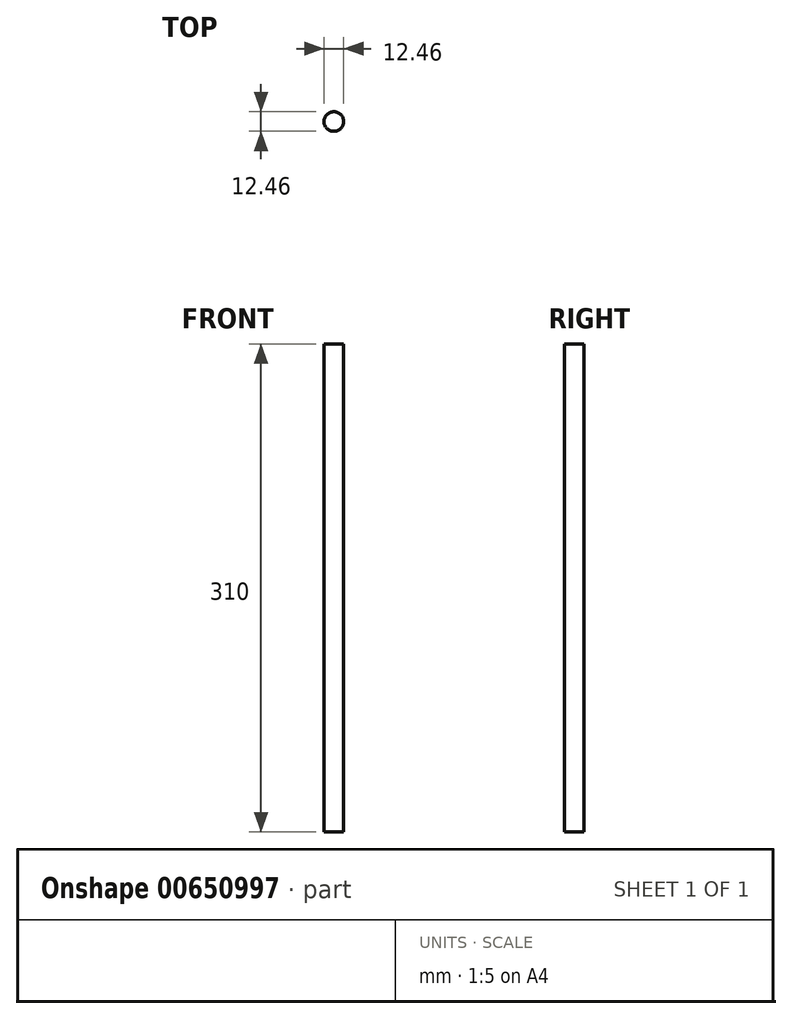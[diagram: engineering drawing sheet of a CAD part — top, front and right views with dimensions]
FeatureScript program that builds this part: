
annotation { "Feature Type Name" : "Feature", "Feature Type Description" : "" }
export const myFeature = defineFeature(function(context is Context, id is Id, definition is map)
    precondition{}
    {
        {
            var Q0;
            Q0=qCreatedBy(makeId("Top.planeOp"),FACE);
            var sketch = newSketch(context, id + "F0", { "sketchPlane" : qUnion([Q0])});
            skCircle(sketch, "E0", {"center": v(-15.14, -11.46) * mm, "radius": 6.23 * mm});
            skSolve(sketch);
        }
        {
            var Q0;
            Q0 = qSketchRegion(id + "F0", true);
            extrude(context, id + "F1", {"entities" : qUnion([Q0]), "depth" : 310 * mm, "offsetDistance" : 25 * mm});
        }
    });
